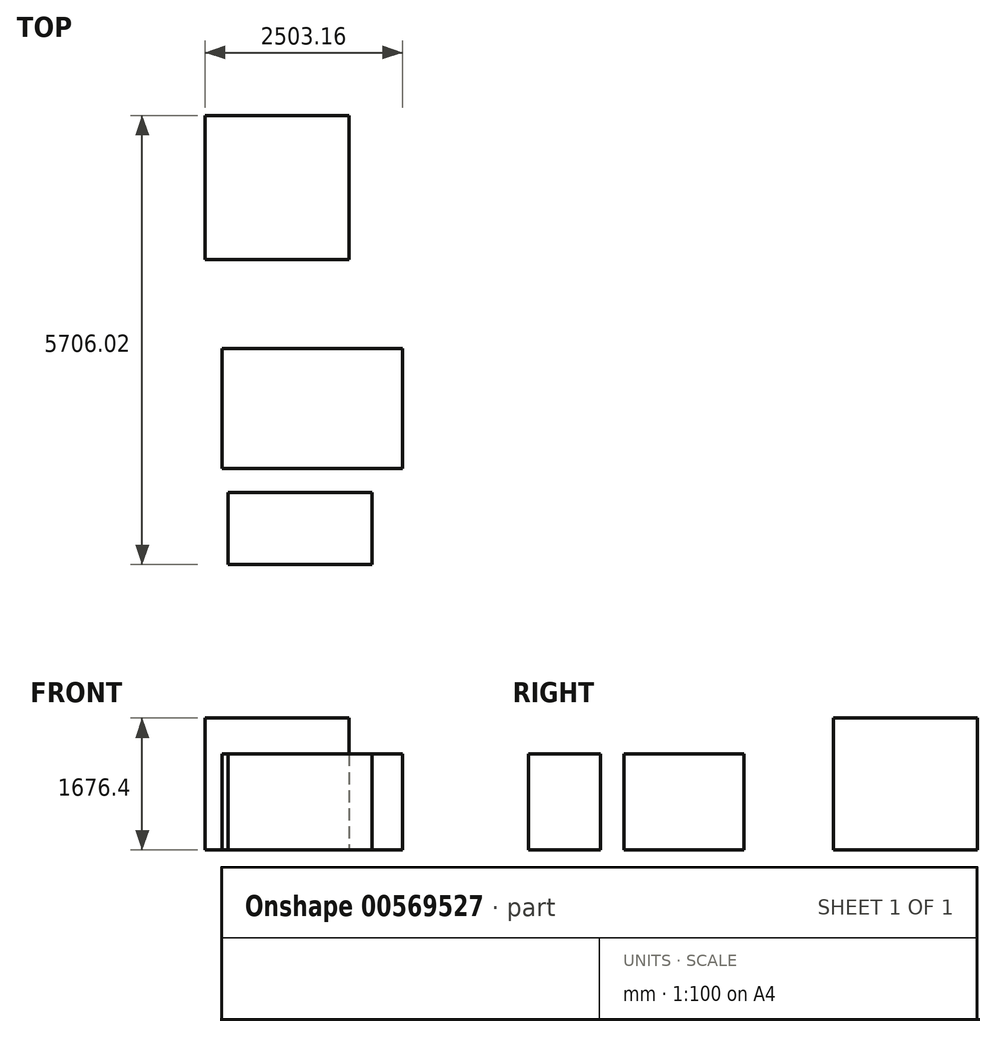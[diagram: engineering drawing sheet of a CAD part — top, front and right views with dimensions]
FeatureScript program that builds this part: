
annotation { "Feature Type Name" : "Feature", "Feature Type Description" : "" }
export const myFeature = defineFeature(function(context is Context, id is Id, definition is map)
    precondition{}
    {
        {
            var Q0;
            Q0=qCreatedBy(makeId("Top.planeOp"),FACE);
            var sketch = newSketch(context, id + "F0", { "sketchPlane" : qUnion([Q0])});
            skLineSegment(sketch, "E0.bottom", {"start": v(813.6, -558.9) * mm, "end": v(-1472.4, -558.9) * mm});
            skLineSegment(sketch, "E0.top", {"start": v(813.6, 965.1) * mm, "end": v(-1472.4, 965.1) * mm});
            skLineSegment(sketch, "E0.left", {"start": v(813.6, -558.9) * mm, "end": v(813.6, 965.1) * mm});
            skLineSegment(sketch, "E0.right", {"start": v(-1472.4, -558.9) * mm, "end": v(-1472.4, 965.1) * mm});
            skSolve(sketch);
        }
        {
            var Q0;
            Q0=makeQuery(id+"F0.imprint","IMPRINT",FACE,{"disambiguationData":[TD([[makeQuery(id+"F0.imprint","IMPRINT",EDGE,{"derivedFrom":sQuery(id+"F0.wireOp",EDGE,"E0.bottom")}),-1.0]])]});
            extrude(context, id + "F1", {"entities" : qUnion([Q0]), "depth" : 1219.2 * mm, "offsetDistance" : 25.4 * mm});
        }
        {
            var Q0;
            Q0=makeQuery(id+"F1.opExtrude","CAP_FACE",FACE,{"disambiguationData":[OSD([sQuery(id+"F0.wireOp",EDGE,"E0.bottom"),sQuery(id+"F0.wireOp",EDGE,"E0.top"),sQuery(id+"F0.wireOp",EDGE,"E0.left"),sQuery(id+"F0.wireOp",EDGE,"E0.right")])],"isStart":false});
            var sketch = newSketch(context, id + "F2", { "sketchPlane" : qUnion([Q0])});
            skLineSegment(sketch, "E1.bottom", {"start": v(427.27, -1777.7) * mm, "end": v(-1401.53, -1777.7) * mm});
            skLineSegment(sketch, "E1.top", {"start": v(427.27, -863.3) * mm, "end": v(-1401.53, -863.3) * mm});
            skLineSegment(sketch, "E1.left", {"start": v(427.27, -1777.7) * mm, "end": v(427.27, -863.3) * mm});
            skLineSegment(sketch, "E1.right", {"start": v(-1401.53, -1777.7) * mm, "end": v(-1401.53, -863.3) * mm});
            skSolve(sketch);
        }
        {
            var Q0;
            Q0=makeQuery(id+"F2.imprint","IMPRINT",FACE,{"disambiguationData":[TD([[makeQuery(id+"F2.imprint","IMPRINT",EDGE,{"derivedFrom":sQuery(id+"F2.wireOp",EDGE,"E1.bottom")}),-1.0]])]});
            extrude(context, id + "F3", {"entities" : qUnion([Q0]), "oppositeDirection" : true, "depth" : 1219.2 * mm, "offsetDistance" : 25.4 * mm});
        }
        {
            var Q0;
            Q0=makeQuery(id+"F1.opExtrude","CAP_FACE",FACE,{"disambiguationData":[OSD([sQuery(id+"F0.wireOp",EDGE,"E0.bottom"),sQuery(id+"F0.wireOp",EDGE,"E0.top"),sQuery(id+"F0.wireOp",EDGE,"E0.left"),sQuery(id+"F0.wireOp",EDGE,"E0.right")])],"isStart":true});
            var sketch = newSketch(context, id + "F4", { "sketchPlane" : qUnion([Q0])});
            skLineSegment(sketch, "E2.bottom", {"start": v(139.25, -2099.51) * mm, "end": v(-1689.55, -2099.51) * mm});
            skLineSegment(sketch, "E2.top", {"start": v(139.25, -3928.31) * mm, "end": v(-1689.55, -3928.31) * mm});
            skLineSegment(sketch, "E2.left", {"start": v(139.25, -2099.51) * mm, "end": v(139.25, -3928.31) * mm});
            skLineSegment(sketch, "E2.right", {"start": v(-1689.55, -2099.51) * mm, "end": v(-1689.55, -3928.31) * mm});
            skSolve(sketch);
        }
        {
            var Q0;
            Q0=makeQuery(id+"F4.imprint","IMPRINT",FACE,{"disambiguationData":[TD([[makeQuery(id+"F4.imprint","IMPRINT",EDGE,{"derivedFrom":sQuery(id+"F4.wireOp",EDGE,"E2.bottom")}),1.0]])]});
            extrude(context, id + "F5", {"entities" : qUnion([Q0]), "oppositeDirection" : true, "depth" : 1676.4 * mm, "offsetDistance" : 25.4 * mm});
        }
    });
